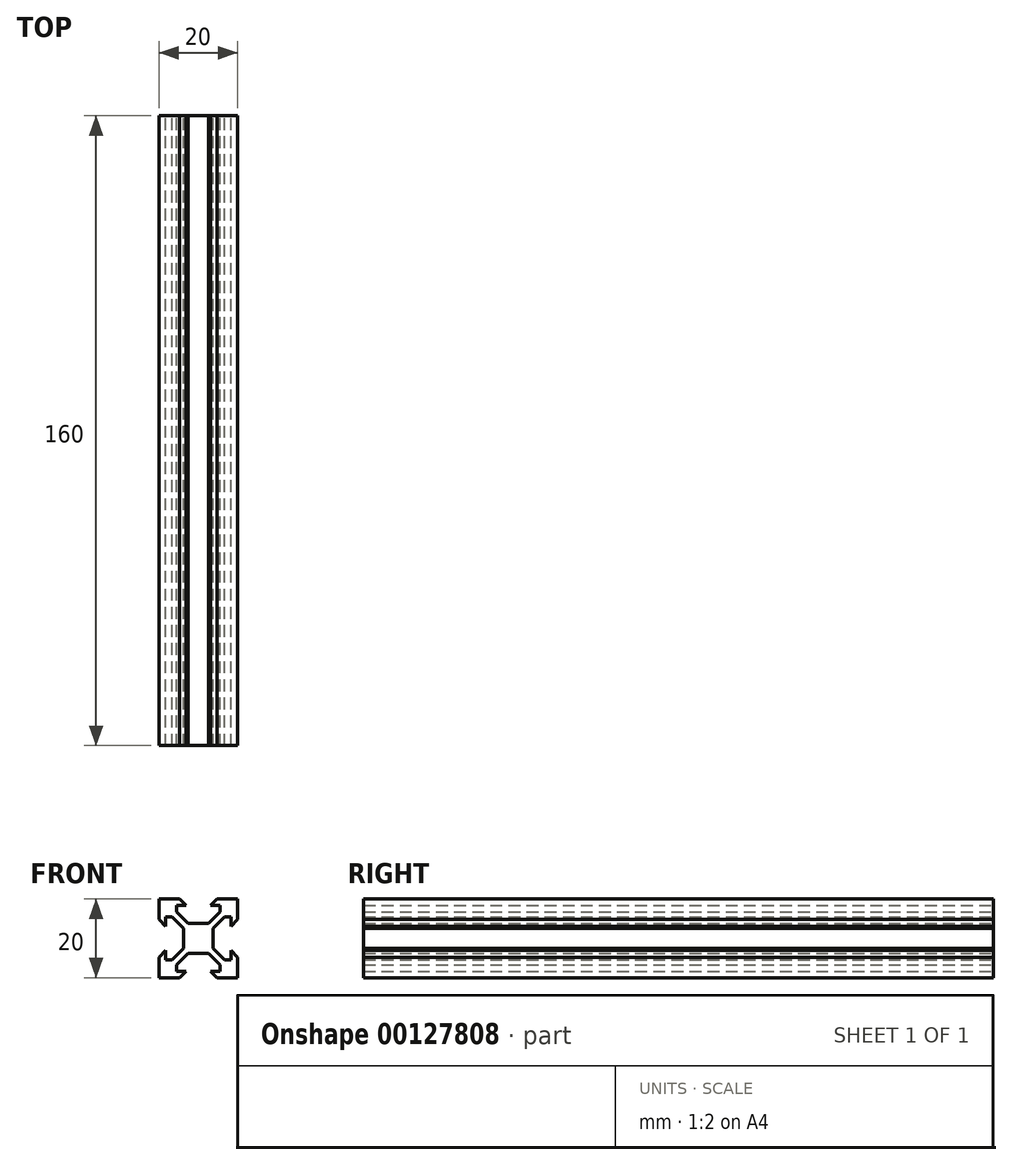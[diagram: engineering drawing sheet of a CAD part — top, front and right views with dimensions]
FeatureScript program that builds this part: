
annotation { "Feature Type Name" : "Feature", "Feature Type Description" : "" }
export const myFeature = defineFeature(function(context is Context, id is Id, definition is map)
    precondition{}
    {
        {
            var Q0;
            Q0=qCreatedBy(makeId("Front.planeOp"),FACE);
            var sketch = newSketch(context, id + "F0", { "sketchPlane" : qUnion([Q0])});
            skLineSegment(sketch, "E0", {"start": v(-10, 10) * mm, "end": v(-4.78, 10) * mm});
            skLineSegment(sketch, "E1", {"start": v(-4.78, 10) * mm, "end": v(-3.1, 8.33) * mm});
            skLineSegment(sketch, "E2", {"start": v(-3.1, 8.32) * mm, "end": v(-5.5, 8.32) * mm});
            skLineSegment(sketch, "E3", {"start": v(-5.5, 8.32) * mm, "end": v(-5.5, 6.68) * mm});
            skLineSegment(sketch, "E4", {"start": v(-5.5, 6.68) * mm, "end": v(-2.57, 3.75) * mm});
            skLineSegment(sketch, "E5", {"start": v(-2.57, 3.75) * mm, "end": v(0, 3.75) * mm});
            skLineSegment(sketch, "E6", {"start": v(0, 0) * mm, "end": v(0, -2.66) * mm, "construction": true});
            skLineSegment(sketch, "E7", {"start": v(0, 0) * mm, "end": v(-3.75, 0) * mm, "construction": true});
            skLineSegment(sketch, "E8", {"start": v(-10, 10) * mm, "end": v(-10, 4.77) * mm});
            skLineSegment(sketch, "E9", {"start": v(-10, 4.78) * mm, "end": v(-8.33, 3.1) * mm});
            skLineSegment(sketch, "E10", {"start": v(-8.32, 3.1) * mm, "end": v(-8.32, 5.5) * mm});
            skLineSegment(sketch, "E11", {"start": v(-8.33, 5.5) * mm, "end": v(-6.68, 5.5) * mm});
            skLineSegment(sketch, "E12", {"start": v(-6.68, 5.5) * mm, "end": v(-3.75, 2.57) * mm});
            skLineSegment(sketch, "E13", {"start": v(-3.75, 2.57) * mm, "end": v(-3.75, 0) * mm});
            skCircle(sketch, "E14", {"center": v(0, 0) * mm, "radius": 2.1 * mm, "construction": true});
            skLineSegment(sketch, "E15.1.0", {"start": v(-5.5, -6.68) * mm, "end": v(-2.57, -3.75) * mm});
            skLineSegment(sketch, "E15.1.1", {"start": v(-5.5, -8.33) * mm, "end": v(-5.5, -6.68) * mm});
            skLineSegment(sketch, "E15.1.2", {"start": v(-3.1, -8.32) * mm, "end": v(-5.5, -8.32) * mm});
            skLineSegment(sketch, "E15.1.3", {"start": v(-4.78, -10) * mm, "end": v(-3.1, -8.33) * mm});
            skLineSegment(sketch, "E15.1.4", {"start": v(-10, -10) * mm, "end": v(-4.77, -10) * mm});
            skLineSegment(sketch, "E15.1.5", {"start": v(-8.32, -5.5) * mm, "end": v(-6.68, -5.5) * mm});
            skLineSegment(sketch, "E15.1.6", {"start": v(-8.32, -3.1) * mm, "end": v(-8.32, -5.5) * mm});
            skLineSegment(sketch, "E15.1.7", {"start": v(-10, -4.77) * mm, "end": v(-8.33, -3.1) * mm});
            skLineSegment(sketch, "E15.1.8", {"start": v(-10, -10) * mm, "end": v(-10, -4.77) * mm});
            skLineSegment(sketch, "E15.1.9", {"start": v(-2.57, -3.75) * mm, "end": v(0, -3.75) * mm});
            skLineSegment(sketch, "E15.1.10", {"start": v(-6.68, -5.5) * mm, "end": v(-3.75, -2.57) * mm});
            skLineSegment(sketch, "E15.1.11", {"start": v(-3.75, -2.57) * mm, "end": v(-3.75, 0) * mm});
            skLineSegment(sketch, "E15.2.0", {"start": v(6.68, -5.5) * mm, "end": v(3.75, -2.57) * mm});
            skLineSegment(sketch, "E15.2.1", {"start": v(8.33, -5.5) * mm, "end": v(6.68, -5.5) * mm});
            skLineSegment(sketch, "E15.2.2", {"start": v(8.32, -3.1) * mm, "end": v(8.32, -5.5) * mm});
            skLineSegment(sketch, "E15.2.3", {"start": v(10, -4.78) * mm, "end": v(8.33, -3.1) * mm});
            skLineSegment(sketch, "E15.2.4", {"start": v(10, -10) * mm, "end": v(10, -4.78) * mm});
            skLineSegment(sketch, "E15.2.5", {"start": v(5.5, -8.32) * mm, "end": v(5.5, -6.68) * mm});
            skLineSegment(sketch, "E15.2.6", {"start": v(3.1, -8.32) * mm, "end": v(5.5, -8.32) * mm});
            skLineSegment(sketch, "E15.2.7", {"start": v(4.77, -10) * mm, "end": v(3.1, -8.33) * mm});
            skLineSegment(sketch, "E15.2.8", {"start": v(10, -10) * mm, "end": v(4.77, -10) * mm});
            skLineSegment(sketch, "E15.2.9", {"start": v(3.75, -2.57) * mm, "end": v(3.75, 0) * mm});
            skLineSegment(sketch, "E15.2.10", {"start": v(5.5, -6.68) * mm, "end": v(2.57, -3.75) * mm});
            skLineSegment(sketch, "E15.2.11", {"start": v(2.57, -3.75) * mm, "end": v(0, -3.75) * mm});
            skLineSegment(sketch, "E15.3.0", {"start": v(5.5, 6.68) * mm, "end": v(2.57, 3.75) * mm});
            skLineSegment(sketch, "E15.3.1", {"start": v(5.5, 8.33) * mm, "end": v(5.5, 6.68) * mm});
            skLineSegment(sketch, "E15.3.2", {"start": v(3.1, 8.32) * mm, "end": v(5.5, 8.32) * mm});
            skLineSegment(sketch, "E15.3.3", {"start": v(4.78, 10) * mm, "end": v(3.1, 8.33) * mm});
            skLineSegment(sketch, "E15.3.4", {"start": v(10, 10) * mm, "end": v(4.78, 10) * mm});
            skLineSegment(sketch, "E15.3.5", {"start": v(8.32, 5.5) * mm, "end": v(6.68, 5.5) * mm});
            skLineSegment(sketch, "E15.3.6", {"start": v(8.32, 3.1) * mm, "end": v(8.32, 5.5) * mm});
            skLineSegment(sketch, "E15.3.7", {"start": v(10, 4.77) * mm, "end": v(8.33, 3.1) * mm});
            skLineSegment(sketch, "E15.3.8", {"start": v(10, 10) * mm, "end": v(10, 4.77) * mm});
            skLineSegment(sketch, "E15.3.9", {"start": v(2.57, 3.75) * mm, "end": v(0, 3.75) * mm});
            skLineSegment(sketch, "E15.3.10", {"start": v(6.68, 5.5) * mm, "end": v(3.75, 2.57) * mm});
            skLineSegment(sketch, "E15.3.11", {"start": v(3.75, 2.57) * mm, "end": v(3.75, 0) * mm});
            skSolve(sketch);
        }
        {
            var Q0;
            Q0=qSketchRegion(id+"F0",true);
            extrude(context, id + "F1", {"entities" : qUnion([Q0]), "endBound" : BoundingType.SYMMETRIC, "depth" : 160 * mm});
        }
    });
